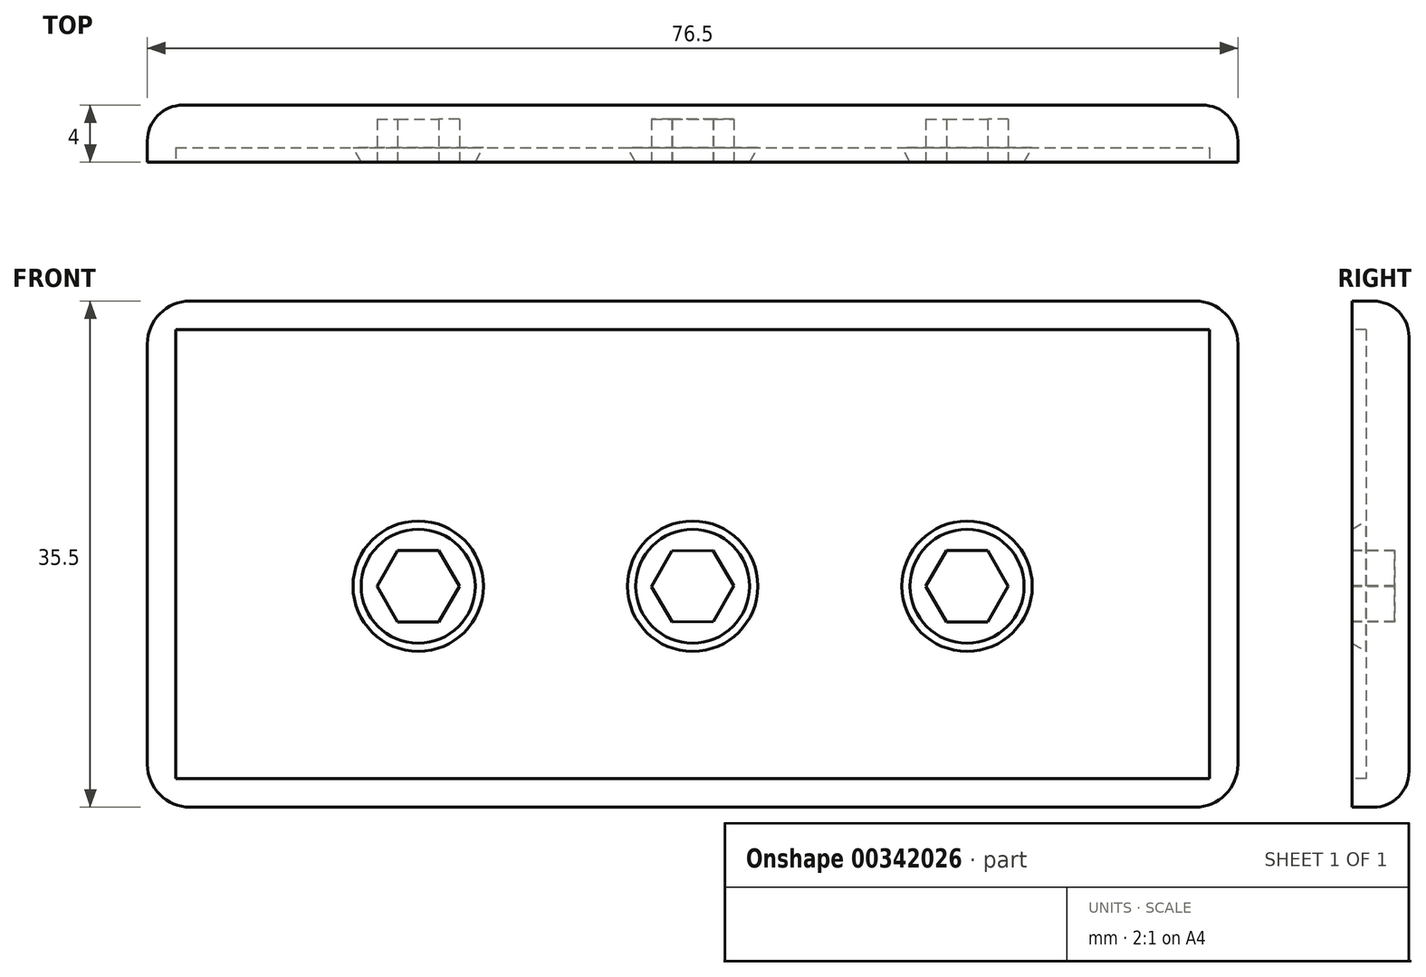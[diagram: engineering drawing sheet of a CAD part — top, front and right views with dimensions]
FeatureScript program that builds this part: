
annotation { "Feature Type Name" : "Feature", "Feature Type Description" : "" }
export const myFeature = defineFeature(function(context is Context, id is Id, definition is map)
    precondition{}
    {
        {
            var Q0;
            Q0=qCreatedBy(makeId("Front.planeOp"),FACE);
            var sketch = newSketch(context, id + "F0", { "sketchPlane" : qUnion([Q0])});
            skLineSegment(sketch, "E0.bottom", {"start": v(-38.25, 17.75) * mm, "end": v(38.25, 17.75) * mm});
            skLineSegment(sketch, "E0.top", {"start": v(-38.25, -17.75) * mm, "end": v(38.25, -17.75) * mm});
            skLineSegment(sketch, "E0.left", {"start": v(-38.25, 17.75) * mm, "end": v(-38.25, -17.75) * mm});
            skLineSegment(sketch, "E0.right", {"start": v(38.25, 17.75) * mm, "end": v(38.25, -17.75) * mm});
            skPoint(sketch, "E0.middle", {"position": v(0, 0) * mm});
            skPoint(sketch, "E1", {"position": v(0, -2.25) * mm});
            skPoint(sketch, "E1.positionSnap0", {"position": v(0, 17.75) * mm});
            skSolve(sketch);
        }
        {
            var Q0;
            Q0=makeQuery(id+"F0.imprint","IMPRINT",FACE,{"disambiguationData":[TD([[makeQuery(id+"F0.imprint","IMPRINT",EDGE,{"derivedFrom":sQuery(id+"F0.wireOp",EDGE,"E0.bottom")}),-1.0]])]});
            extrude(context, id + "F1", {"entities" : qUnion([Q0]), "depth" : 4 * mm});
        }
        {
            var Q0;
            Q0=makeQuery(id+"F1.opExtrude","CAP_FACE",FACE,{"disambiguationData":[OSD([sQuery(id+"F0.wireOp",EDGE,"E0.bottom"),sQuery(id+"F0.wireOp",EDGE,"E0.top"),sQuery(id+"F0.wireOp",EDGE,"E0.left"),sQuery(id+"F0.wireOp",EDGE,"E0.right")])],"isStart":false});
            var sketch = newSketch(context, id + "F2", { "sketchPlane" : qUnion([Q0])});
            skPoint(sketch, "E2", {"position": v(-36.25, 15.75) * mm});
            skLineSegment(sketch, "E3.bottom", {"start": v(-36.25, 15.75) * mm, "end": v(36.25, 15.75) * mm});
            skLineSegment(sketch, "E3.top", {"start": v(-36.25, -15.75) * mm, "end": v(36.25, -15.75) * mm});
            skLineSegment(sketch, "E3.left", {"start": v(-36.25, 15.75) * mm, "end": v(-36.25, -15.75) * mm});
            skLineSegment(sketch, "E3.right", {"start": v(36.25, 15.75) * mm, "end": v(36.25, -15.75) * mm});
            skPoint(sketch, "E3.middle", {"position": v(0, 0) * mm});
            skSolve(sketch);
        }
        {
            var Q0;
            Q0=makeQuery(id+"F2.imprint","IMPRINT",FACE,{"disambiguationData":[TD([[makeQuery(id+"F2.imprint","IMPRINT",EDGE,{"derivedFrom":sQuery(id+"F2.wireOp",EDGE,"E3.bottom")}),-1.0]])]});
            extrude(context, id + "F3", {"entities" : qUnion([Q0]), "operationType" : NewBodyOperationType.REMOVE, "oppositeDirection" : true, "depth" : 1 * mm});
        }
        {
            var Q0;
            Q0=makeQuery(id+"F3.boolean.opBoolean","COPY",FACE,{"derivedFrom":makeQuery(id+"F3.opExtrude","CAP_FACE",FACE,{"disambiguationData":[OSD([sQuery(id+"F2.wireOp",EDGE,"E3.bottom"),sQuery(id+"F2.wireOp",EDGE,"E3.top"),sQuery(id+"F2.wireOp",EDGE,"E3.left"),sQuery(id+"F2.wireOp",EDGE,"E3.right")])],"isStart":false})});
            var sketch = newSketch(context, id + "F4", { "sketchPlane" : qUnion([Q0])});
            skPoint(sketch, "E4", {"position": v(0, -2.25) * mm});
            skSolve(sketch);
        }
        {
            var Q0;
            Q0=makeQuery(id+"F3.boolean.opBoolean","COPY",FACE,{"derivedFrom":makeQuery(id+"F3.opExtrude","CAP_FACE",FACE,{"disambiguationData":[OSD([sQuery(id+"F2.wireOp",EDGE,"E3.bottom"),sQuery(id+"F2.wireOp",EDGE,"E3.top"),sQuery(id+"F2.wireOp",EDGE,"E3.left"),sQuery(id+"F2.wireOp",EDGE,"E3.right")])],"isStart":false})});
            var sketch = newSketch(context, id + "F5", { "sketchPlane" : qUnion([Q0])});
            skPoint(sketch, "E5", {"position": v(0, -2.25) * mm});
            skCircle(sketch, "E6", {"center": v(0, -2.25) * mm, "radius": 6 * mm});
            skSolve(sketch);
        }
        {
            var Q0;
            Q0=makeQuery(id+"F4.imprint","IMPRINT",FACE,{"disambiguationData":[TD([[makeQuery(id+"F4.imprint","IMPRINT",EDGE,{"derivedFrom":makeQuery(id+"F3.boolean.opBoolean","COPY",EDGE,{"derivedFrom":makeQuery(id+"F3.opExtrude","CAP_EDGE",EDGE,{"disambiguationData":[OSD([sQuery(id+"F2.wireOp",EDGE,"E3.bottom")])],"isStart":false})})}),-1.0]])]});
            var sketch = newSketch(context, id + "F6", { "sketchPlane" : qUnion([Q0])});
            skPoint(sketch, "E7", {"position": v(19.25, -2.25) * mm});
            skPoint(sketch, "E8", {"position": v(-19.25, -2.25) * mm});
            skCircle(sketch, "E9", {"center": v(19.25, -2.25) * mm, "radius": 6 * mm});
            skCircle(sketch, "E10", {"center": v(-19.25, -2.25) * mm, "radius": 6 * mm});
            skSolve(sketch);
        }
        {
            var Q0;
            Q0=makeQuery(id+"F5.imprint","IMPRINT",FACE,{"disambiguationData":[TD([[makeQuery(id+"F5.imprint","IMPRINT",EDGE,{"derivedFrom":sQuery(id+"F5.wireOp",EDGE,"E6")}),1.0]])]});
            extrude(context, id + "F7", {"entities" : qUnion([Q0]), "operationType" : NewBodyOperationType.ADD, "depth" : 1 * mm});
        }
        {
            var Q0;
            Q0 = qSketchRegion(id + "F6", true);
            extrude(context, id + "F8", {"entities" : qUnion([Q0]), "operationType" : NewBodyOperationType.ADD, "depth" : 1 * mm});
        }
        {
            var Q0;
            Q0=makeQuery(id+"F7.opExtrude","CAP_EDGE",EDGE,{"disambiguationData":[OSD([sQuery(id+"F5.wireOp",EDGE,"E6")])],"isStart":false});
            var Q1;
            Q1=makeQuery(id+"F8.opExtrude","CAP_EDGE",EDGE,{"disambiguationData":[OSD([sQuery(id+"F6.wireOp",EDGE,"E10")])],"isStart":false});
            var Q2;
            Q2=makeQuery(id+"F8.opExtrude","CAP_EDGE",EDGE,{"disambiguationData":[OSD([sQuery(id+"F6.wireOp",EDGE,"E9")])],"isStart":false});
            chamfer(context, id + "F9", {"entities" : qUnion([Q0, Q1, Q2]), "chamferType" : ChamferType.TWO_OFFSETS, "width1" : 2 * mm, "oppositeDirection" : false, "width2" : 3.5 * mm, "tangentPropagation" : true});
        }
        {
            var Q0;
            Q0=makeQuery(id+"F7.opExtrude","CAP_FACE",FACE,{"disambiguationData":[OSD([sQuery(id+"F5.wireOp",EDGE,"E6")])],"isStart":false});
            var sketch = newSketch(context, id + "F10", { "sketchPlane" : qUnion([Q0])});
            skCircle(sketch, "E11.cCircle", {"center": v(0, -2.25) * mm, "radius": 2.5 * mm, "construction": true});
            skLineSegment(sketch, "E11.0", {"start": v(-2.89, -2.27) * mm, "end": v(-1.46, 0.24) * mm});
            skLineSegment(sketch, "E11.1", {"start": v(-1.46, 0.24) * mm, "end": v(1.42, 0.26) * mm});
            skLineSegment(sketch, "E11.2", {"start": v(1.42, 0.26) * mm, "end": v(2.89, -2.23) * mm});
            skLineSegment(sketch, "E11.3", {"start": v(2.89, -2.23) * mm, "end": v(1.46, -4.74) * mm});
            skLineSegment(sketch, "E11.4", {"start": v(1.46, -4.74) * mm, "end": v(-1.42, -4.76) * mm});
            skLineSegment(sketch, "E11.5", {"start": v(-1.42, -4.76) * mm, "end": v(-2.89, -2.27) * mm});
            skPoint(sketch, "E11.0.midPoint", {"position": v(-2.18, -1.02) * mm});
            skSolve(sketch);
        }
        {
            var Q0;
            Q0=makeQuery(id+"F8.opExtrude","CAP_FACE",FACE,{"disambiguationData":[OSD([sQuery(id+"F6.wireOp",EDGE,"E9")])],"isStart":false});
            var sketch = newSketch(context, id + "F11", { "sketchPlane" : qUnion([Q0])});
            skCircle(sketch, "E12.cCircle", {"center": v(19.25, -2.25) * mm, "radius": 2.5 * mm, "construction": true});
            skLineSegment(sketch, "E12.0", {"start": v(17.8, 0.25) * mm, "end": v(20.7, 0.25) * mm});
            skLineSegment(sketch, "E12.1", {"start": v(20.7, 0.25) * mm, "end": v(22.14, -2.25) * mm});
            skLineSegment(sketch, "E12.2", {"start": v(22.14, -2.25) * mm, "end": v(20.7, -4.75) * mm});
            skLineSegment(sketch, "E12.3", {"start": v(20.7, -4.75) * mm, "end": v(17.8, -4.75) * mm});
            skLineSegment(sketch, "E12.4", {"start": v(17.8, -4.75) * mm, "end": v(16.36, -2.25) * mm});
            skLineSegment(sketch, "E12.5", {"start": v(16.36, -2.25) * mm, "end": v(17.8, 0.25) * mm});
            skPoint(sketch, "E12.0.midPoint", {"position": v(19.25, 0.25) * mm});
            skSolve(sketch);
        }
        {
            var Q0;
            Q0=makeQuery(id+"F8.opExtrude","CAP_FACE",FACE,{"disambiguationData":[OSD([sQuery(id+"F6.wireOp",EDGE,"E10")])],"isStart":false});
            var sketch = newSketch(context, id + "F12", { "sketchPlane" : qUnion([Q0])});
            skCircle(sketch, "E13.cCircle", {"center": v(-19.25, -2.25) * mm, "radius": 2.5 * mm, "construction": true});
            skLineSegment(sketch, "E13.0", {"start": v(-20.7, 0.25) * mm, "end": v(-17.8, 0.25) * mm});
            skLineSegment(sketch, "E13.1", {"start": v(-17.8, 0.25) * mm, "end": v(-16.36, -2.25) * mm});
            skLineSegment(sketch, "E13.2", {"start": v(-16.36, -2.25) * mm, "end": v(-17.8, -4.75) * mm});
            skLineSegment(sketch, "E13.3", {"start": v(-17.8, -4.75) * mm, "end": v(-20.7, -4.75) * mm});
            skLineSegment(sketch, "E13.4", {"start": v(-20.7, -4.75) * mm, "end": v(-22.14, -2.25) * mm});
            skLineSegment(sketch, "E13.5", {"start": v(-22.14, -2.25) * mm, "end": v(-20.7, 0.25) * mm});
            skPoint(sketch, "E13.0.midPoint", {"position": v(-19.25, 0.25) * mm});
            skSolve(sketch);
        }
        {
            var Q0;
            Q0=makeQuery(id+"F10.imprint","IMPRINT",FACE,{"disambiguationData":[TD([[makeQuery(id+"F10.imprint","IMPRINT",EDGE,{"derivedFrom":sQuery(id+"F10.wireOp",EDGE,"E11.0")}),-1.0]])]});
            var Q1;
            Q1=makeQuery(id+"F12.imprint","IMPRINT",FACE,{"disambiguationData":[TD([[makeQuery(id+"F12.imprint","IMPRINT",EDGE,{"derivedFrom":sQuery(id+"F12.wireOp",EDGE,"E13.0")}),-1.0]])]});
            var Q2;
            Q2=makeQuery(id+"F11.imprint","IMPRINT",FACE,{"disambiguationData":[TD([[makeQuery(id+"F11.imprint","IMPRINT",EDGE,{"derivedFrom":sQuery(id+"F11.wireOp",EDGE,"E12.0")}),-1.0]])]});
            extrude(context, id + "F13", {"entities" : qUnion([Q0, Q1, Q2]), "operationType" : NewBodyOperationType.REMOVE, "oppositeDirection" : true, "depth" : 3 * mm});
        }
        {
            var Q0;
            Q0=makeQuery(id+"F1.opExtrude","CAP_EDGE",EDGE,{"disambiguationData":[OSD([sQuery(id+"F0.wireOp",EDGE,"E0.bottom")])],"isStart":true});
            var Q1;
            Q1=makeQuery(id+"F1.opExtrude","CAP_EDGE",EDGE,{"disambiguationData":[OSD([sQuery(id+"F0.wireOp",EDGE,"E0.right")])],"isStart":true});
            var Q2;
            Q2=makeQuery(id+"F1.opExtrude","CAP_EDGE",EDGE,{"disambiguationData":[OSD([sQuery(id+"F0.wireOp",EDGE,"E0.top")])],"isStart":true});
            var Q3;
            Q3=makeQuery(id+"F1.opExtrude","CAP_EDGE",EDGE,{"disambiguationData":[OSD([sQuery(id+"F0.wireOp",EDGE,"E0.left")])],"isStart":true});
            fillet(context, id + "F14", {"entities" : qUnion([Q0, Q1, Q2, Q3]), "radius" : 2.5 * mm, "tangentPropagation" : true, "allowEdgeOverflow" : false});
        }
        {
            var Q0;
            Q0=makeQuery(id+"F14.opFillet","BLEND_EDGE",EDGE,{"blendedFrom":[makeQuery(id+"F1.opExtrude","CAP_EDGE",EDGE,{"disambiguationData":[OSD([sQuery(id+"F0.wireOp",EDGE,"E0.bottom")])],"isStart":true}),makeQuery(id+"F1.opExtrude","CAP_EDGE",EDGE,{"disambiguationData":[OSD([sQuery(id+"F0.wireOp",EDGE,"E0.right")])],"isStart":true})],"blendedInto":[]});
            var Q1;
            Q1=makeQuery(id+"F1.opExtrude","SWEPT_EDGE",EDGE,{"disambiguationData":[OSD([sQuery(id+"F0.wireOp",EDGE,"E0.bottom"),sQuery(id+"F0.wireOp",EDGE,"E0.right")])]});
            var Q2;
            Q2=makeQuery(id+"F1.opExtrude","SWEPT_EDGE",EDGE,{"disambiguationData":[OSD([sQuery(id+"F0.wireOp",EDGE,"E0.top"),sQuery(id+"F0.wireOp",EDGE,"E0.right")])]});
            var Q3;
            Q3=makeQuery(id+"F14.opFillet","BLEND_EDGE",EDGE,{"blendedFrom":[makeQuery(id+"F1.opExtrude","CAP_EDGE",EDGE,{"disambiguationData":[OSD([sQuery(id+"F0.wireOp",EDGE,"E0.top")])],"isStart":true}),makeQuery(id+"F1.opExtrude","CAP_EDGE",EDGE,{"disambiguationData":[OSD([sQuery(id+"F0.wireOp",EDGE,"E0.right")])],"isStart":true})],"blendedInto":[]});
            var Q4;
            Q4=makeQuery(id+"F1.opExtrude","SWEPT_EDGE",EDGE,{"disambiguationData":[OSD([sQuery(id+"F0.wireOp",EDGE,"E0.bottom"),sQuery(id+"F0.wireOp",EDGE,"E0.left")])]});
            var Q5;
            Q5=makeQuery(id+"F14.opFillet","BLEND_EDGE",EDGE,{"blendedFrom":[makeQuery(id+"F1.opExtrude","CAP_EDGE",EDGE,{"disambiguationData":[OSD([sQuery(id+"F0.wireOp",EDGE,"E0.bottom")])],"isStart":true}),makeQuery(id+"F1.opExtrude","CAP_EDGE",EDGE,{"disambiguationData":[OSD([sQuery(id+"F0.wireOp",EDGE,"E0.left")])],"isStart":true})],"blendedInto":[]});
            var Q6;
            Q6=makeQuery(id+"F14.opFillet","BLEND_EDGE",EDGE,{"blendedFrom":[makeQuery(id+"F1.opExtrude","CAP_EDGE",EDGE,{"disambiguationData":[OSD([sQuery(id+"F0.wireOp",EDGE,"E0.top")])],"isStart":true}),makeQuery(id+"F1.opExtrude","CAP_EDGE",EDGE,{"disambiguationData":[OSD([sQuery(id+"F0.wireOp",EDGE,"E0.left")])],"isStart":true})],"blendedInto":[]});
            var Q7;
            Q7=makeQuery(id+"F1.opExtrude","SWEPT_EDGE",EDGE,{"disambiguationData":[OSD([sQuery(id+"F0.wireOp",EDGE,"E0.top"),sQuery(id+"F0.wireOp",EDGE,"E0.left")])]});
            fillet(context, id + "F15", {"entities" : qUnion([Q0, Q1, Q2, Q3, Q4, Q5, Q6, Q7]), "radius" : 3 * mm, "tangentPropagation" : true, "allowEdgeOverflow" : false});
        }
    });
